# Revit family: PA692SGRH Argo Plus
name_source: partatom
category: Mobiliario
units: mm (PartAtom-declared; Revit-internal decimal feet)

## family parameters
Compartido = No
Corte con vacíos al cargar = No
Número OmniClass = 23.40.20.00
Punto de cálculo de habitación = No
Se basa en plano de trabajo = No
Siempre vertical = Sí
Título OmniClass = General Furniture and Specialties

## types (1)
- PA692SGRH Papelera Argo Plus
    Acabado Papelera = Color Gris RAL 9006
    Accessibilidad = Sí
    Altura = 1024 mm  [stored 3.35958 ft]
    Ancho = 400 mm  [stored 1.31234 ft]
    Comentarios de tipo = Cubeta de acaero galvanizada reforzada con ventanillas realizadas con láser, con tratamiento Ferrus, proceso protector del hierro que garantiza una óptima resistencia a la corrosión.Imprimación epoxi y pintura poliéster en polvo color gris RAL 9006.
    Fabricante = BENITO
    Ficha tecnica = http://www.benito.com
    Instalación = Anclaje recomenadado, mediante 3 tornillos de expansión, diámetro 10 .No suministrados
    Material Papelera = Acero
    Modelo = Papelera Argo Plus
    Referencia = PA692SGRH
    URL = https://www.benito.com
    URL Producto = http://www.benito.com

note: [stored X ft] marks values corroborated as IEEE doubles in the binary element streams (Revit-internal decimal feet)

## geometry (parser evidence)
native form markers: Blend x4
no freeform markers — native parametric forms only
